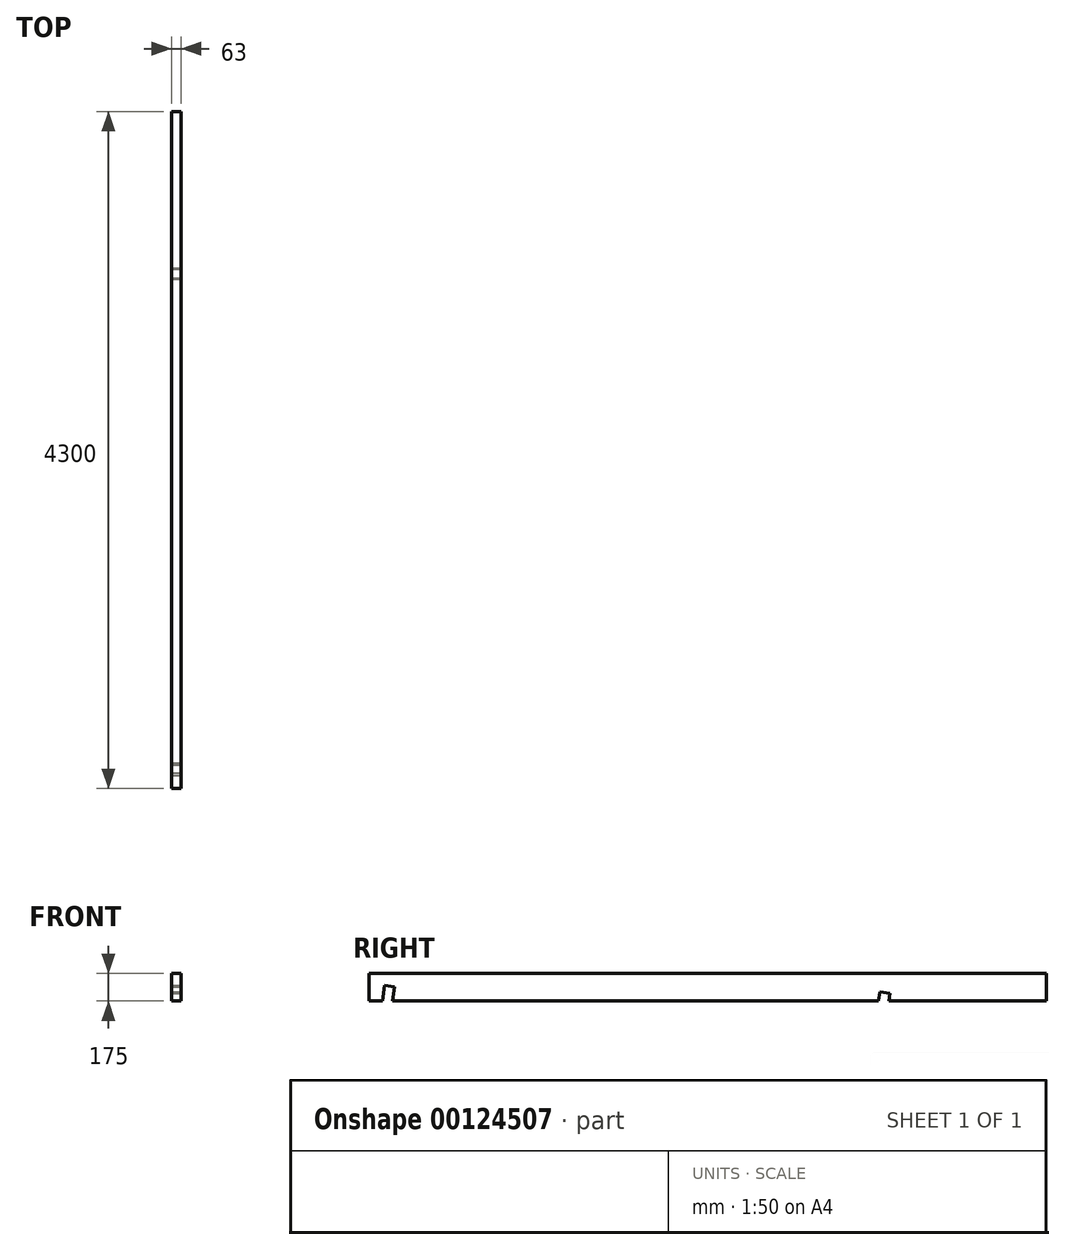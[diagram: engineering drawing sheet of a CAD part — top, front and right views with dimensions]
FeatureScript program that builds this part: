
annotation { "Feature Type Name" : "Feature", "Feature Type Description" : "" }
export const myFeature = defineFeature(function(context is Context, id is Id, definition is map)
    precondition{}
    {
        {
            var Q0;
            Q0=qCreatedBy(makeId("Front.planeOp"),FACE);
            var sketch = newSketch(context, id + "F0", { "sketchPlane" : qUnion([Q0])});
            skLineSegment(sketch, "E0.bottom", {"start": v(31.5, 87.5) * mm, "end": v(-31.5, 87.5) * mm});
            skLineSegment(sketch, "E0.top", {"start": v(31.5, -87.5) * mm, "end": v(-31.5, -87.5) * mm});
            skLineSegment(sketch, "E0.left", {"start": v(31.5, 87.5) * mm, "end": v(31.5, -87.5) * mm});
            skLineSegment(sketch, "E0.right", {"start": v(-31.5, 87.5) * mm, "end": v(-31.5, -87.5) * mm});
            skPoint(sketch, "E0.middle", {"position": v(0, 0) * mm});
            skSolve(sketch);
        }
        {
            var Q0;
            Q0 = qSketchRegion(id + "F0", true);
            extrude(context, id + "F1", {"entities" : qUnion([Q0]), "endBound" : BoundingType.SYMMETRIC, "depth" : 4300 * mm});
        }
        {
            var Q0;
            Q0=makeQuery(id+"F1.opExtrude","SWEPT_FACE",FACE,{"disambiguationData":[OSD([sQuery(id+"F0.wireOp",EDGE,"E0.left")])]});
            var sketch = newSketch(context, id + "F2", { "sketchPlane" : qUnion([Q0])});
            skLineSegment(sketch, "E1", {"start": v(1150, -87.5) * mm, "end": v(1157.03, -37.5) * mm});
            skLineSegment(sketch, "E2", {"start": v(1157.03, -37.5) * mm, "end": v(1092.66, -28.45) * mm});
            skLineSegment(sketch, "E3", {"start": v(1092.66, -28.45) * mm, "end": v(1084.36, -87.5) * mm});
            skLineSegment(sketch, "E4", {"start": v(1084.36, -87.5) * mm, "end": v(1150, -87.5) * mm});
            skLineSegment(sketch, "E5", {"start": v(-2000.66, -87.5) * mm, "end": v(-1988.01, 2.5) * mm});
            skLineSegment(sketch, "E6", {"start": v(-1988.01, 2.5) * mm, "end": v(-2052.38, 11.55) * mm});
            skLineSegment(sketch, "E7", {"start": v(-2052.38, 11.55) * mm, "end": v(-2066.3, -87.5) * mm});
            skLineSegment(sketch, "E8", {"start": v(-2066.3, -87.5) * mm, "end": v(-2000.66, -87.5) * mm});
            skSolve(sketch);
        }
        {
            var Q0;
            Q0 = qSketchRegion(id + "F2", true);
            extrude(context, id + "F3", {"entities" : qUnion([Q0]), "operationType" : NewBodyOperationType.REMOVE, "endBound" : BoundingType.UP_TO_NEXT, "oppositeDirection" : true, "depth" : 25 * mm});
        }
    });
